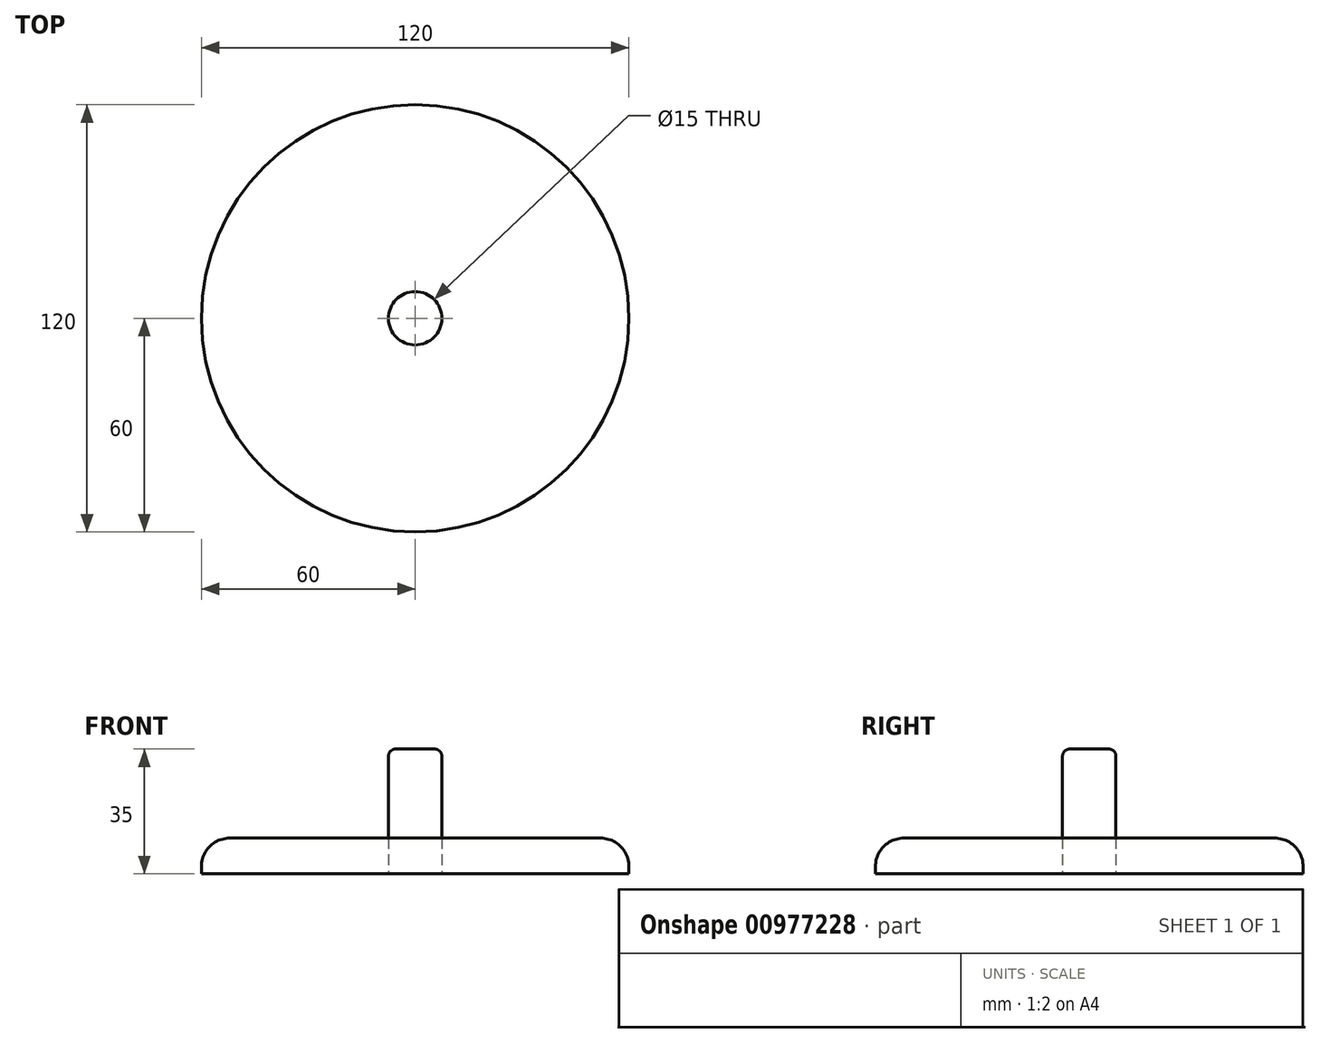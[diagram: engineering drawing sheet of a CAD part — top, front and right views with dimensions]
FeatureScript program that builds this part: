
annotation { "Feature Type Name" : "Feature", "Feature Type Description" : "" }
export const myFeature = defineFeature(function(context is Context, id is Id, definition is map)
    precondition{}
    {
        {
            var Q0;
            Q0=qCreatedBy(makeId("Top.planeOp"),FACE);
            var sketch = newSketch(context, id + "F0", { "sketchPlane" : qUnion([Q0])});
            skCircle(sketch, "E0", {"center": v(0, 0) * mm, "radius": 60 * mm});
            skCircle(sketch, "E1", {"center": v(0, 0) * mm, "radius": 7.5 * mm});
            skSolve(sketch);
        }
        {
            var Q0;
            Q0=makeQuery(id+"F0.imprint","IMPRINT",FACE,{"disambiguationData":[TD([[makeQuery(id+"F0.imprint","IMPRINT",EDGE,{"derivedFrom":sQuery(id+"F0.wireOp",EDGE,"E1")}),1.0]])]});
            var Q1;
            Q1=sQuery(id+"F0.wireOp",EDGE,"E1");
            extrude(context, id + "F1", {"entities" : qUnion([Q0]), "surfaceEntities" : qUnion([Q1]), "depth" : 35 * mm, "offsetDistance" : 25 * mm});
        }
        {
            var Q0;
            Q0=makeQuery(id+"F0.imprint","IMPRINT",FACE,{"disambiguationData":[TD([[makeQuery(id+"F0.imprint","IMPRINT",EDGE,{"derivedFrom":sQuery(id+"F0.wireOp",EDGE,"E0")}),1.0]])]});
            var Q1;
            Q1=sQuery(id+"F0.wireOp",EDGE,"E0");
            extrude(context, id + "F2", {"entities" : qUnion([Q0]), "surfaceEntities" : qUnion([Q1]), "depth" : 10 * mm, "offsetDistance" : 25 * mm});
        }
        {
            var Q0;
            Q0=makeQuery(id+"F1.opExtrude","CAP_EDGE",EDGE,{"disambiguationData":[OSD([sQuery(id+"F0.wireOp",EDGE,"E1")])],"isStart":false});
            fillet(context, id + "F3", {"entities" : qUnion([Q0]), "radius" : 2 * mm, "tangentPropagation" : true, "allowEdgeOverflow" : false});
        }
        {
            var Q0;
            Q0=makeQuery(id+"F2.opExtrude","CAP_EDGE",EDGE,{"disambiguationData":[OSD([sQuery(id+"F0.wireOp",EDGE,"E0")])],"isStart":false});
            fillet(context, id + "F4", {"entities" : qUnion([Q0]), "radius" : 8 * mm, "tangentPropagation" : true, "allowEdgeOverflow" : false});
        }
    });
